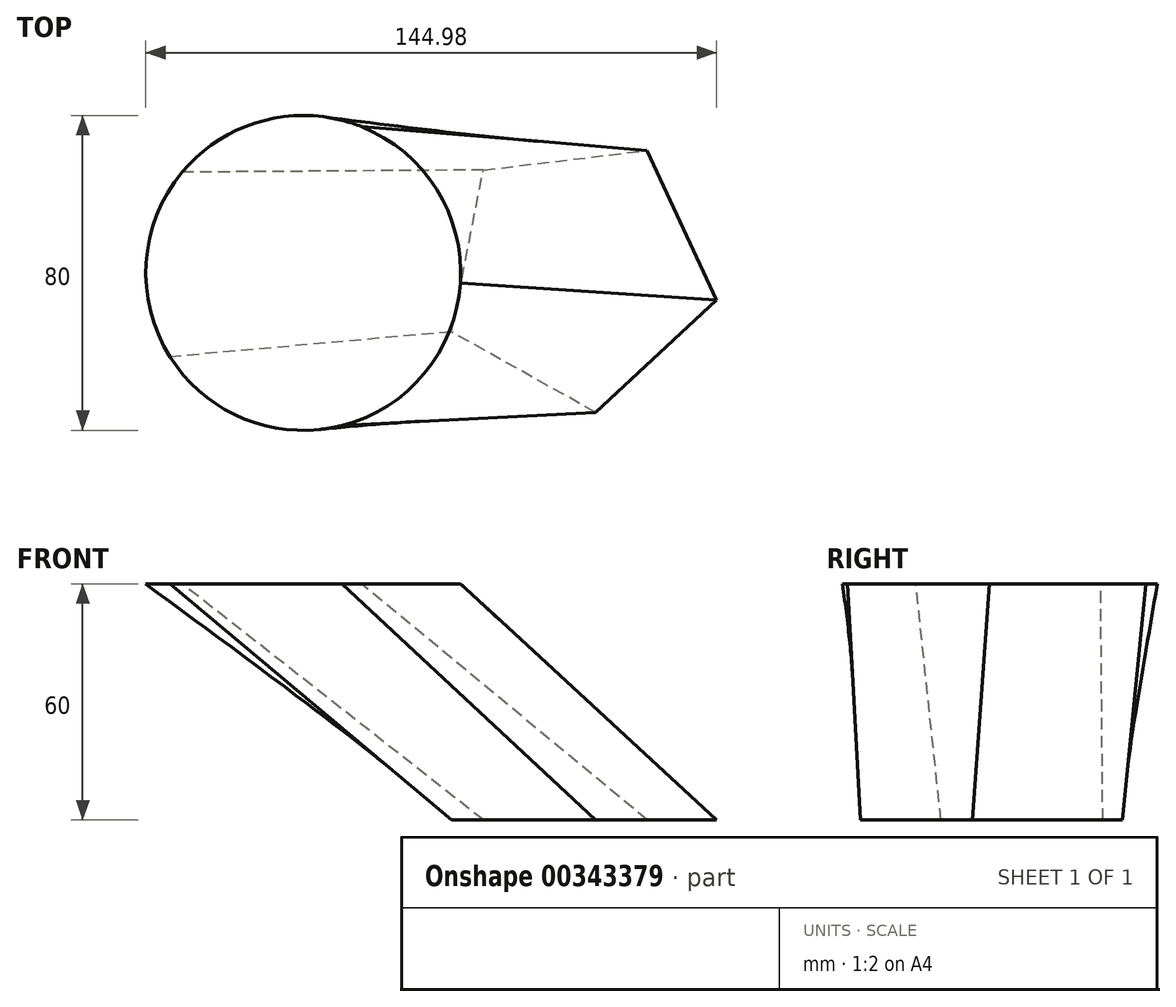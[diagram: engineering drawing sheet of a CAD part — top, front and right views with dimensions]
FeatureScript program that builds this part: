
annotation { "Feature Type Name" : "Feature", "Feature Type Description" : "" }
export const myFeature = defineFeature(function(context is Context, id is Id, definition is map)
    precondition{}
    {
        {
            var Q0;
            Q0=qCreatedBy(makeId("Top.planeOp"),FACE);
            var sketch = newSketch(context, id + "F0", { "sketchPlane" : qUnion([Q0])});
            skCircle(sketch, "E0.cCircle", {"center": v(0, 0) * mm, "radius": 28.85 * mm, "construction": true});
            skLineSegment(sketch, "E0.0", {"start": v(34.98, -6.91) * mm, "end": v(4.24, -35.4) * mm});
            skLineSegment(sketch, "E0.1", {"start": v(4.24, -35.4) * mm, "end": v(-32.36, -14.97) * mm});
            skLineSegment(sketch, "E0.2", {"start": v(-32.36, -14.97) * mm, "end": v(-24.24, 26.15) * mm});
            skLineSegment(sketch, "E0.3", {"start": v(-24.24, 26.15) * mm, "end": v(17.38, 31.13) * mm});
            skLineSegment(sketch, "E0.4", {"start": v(17.38, 31.13) * mm, "end": v(34.98, -6.91) * mm});
            skPoint(sketch, "E0.0.midPoint", {"position": v(19.6, -21.16) * mm});
            skSolve(sketch);
        }
        {
            var Q0;
            Q0=qCreatedBy(makeId("Top.planeOp"),FACE);
            cPlane(context, id + "F1", {"entities" : qUnion([Q0]), "cplaneType" : CPlaneType.OFFSET, "offset" : 60 * mm, "width" : 150 * mm, "height" : 150 * mm});
        }
        {
            var Q0;
            Q0=qCreatedBy(id+"F1.planeOp",FACE);
            var sketch = newSketch(context, id + "F2", { "sketchPlane" : qUnion([Q0])});
            skLineSegment(sketch, "E1", {"start": v(0, 0) * mm, "end": v(-70, 0) * mm, "construction": true});
            skCircle(sketch, "E2", {"center": v(-70, 0) * mm, "radius": 40 * mm});
            skSolve(sketch);
        }
        {
            var Q0;
            Q0=makeQuery(id+"F0.imprint","IMPRINT",FACE,{"disambiguationData":[TD([[makeQuery(id+"F0.imprint","IMPRINT",EDGE,{"derivedFrom":sQuery(id+"F0.wireOp",EDGE,"E0.0")}),-1.0]])]});
            var Q1;
            Q1=makeQuery(id+"F2.imprint","IMPRINT",FACE,{"disambiguationData":[TD([[makeQuery(id+"F2.imprint","IMPRINT",EDGE,{"derivedFrom":sQuery(id+"F2.wireOp",EDGE,"E2")}),1.0]])]});
            loft(context, id + "F3", {"sheetProfilesArray" : [{ "sheetProfileEntities" : qUnion([Q0]) }, { "sheetProfileEntities" : qUnion([Q1]) }]});
        }
    });
